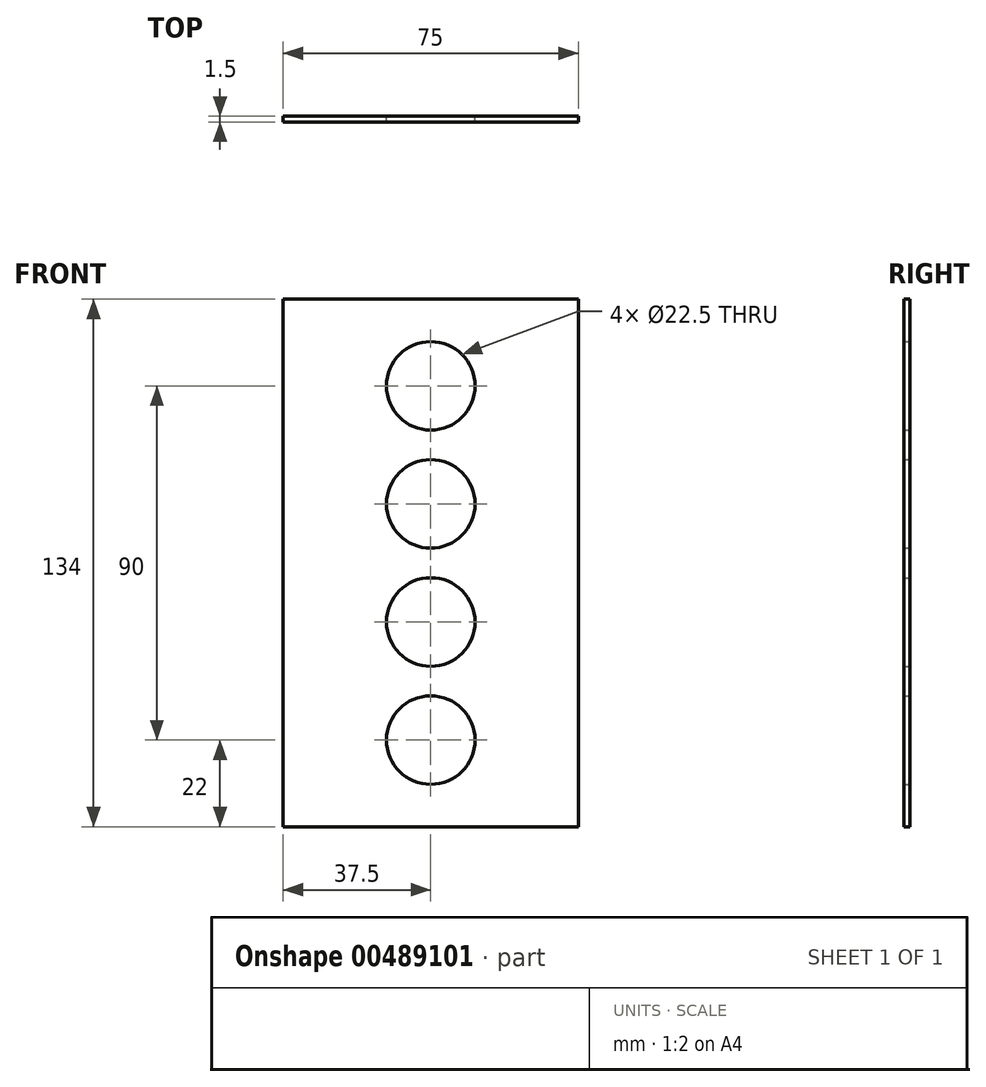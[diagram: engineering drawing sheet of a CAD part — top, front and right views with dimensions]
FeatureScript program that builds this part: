
annotation { "Feature Type Name" : "Feature", "Feature Type Description" : "" }
export const myFeature = defineFeature(function(context is Context, id is Id, definition is map)
    precondition{}
    {
        {
            var Q0;
            Q0=qCreatedBy(makeId("Front.planeOp"),FACE);
            var sketch = newSketch(context, id + "F0", { "sketchPlane" : qUnion([Q0])});
            skLineSegment(sketch, "E0.bottom", {"start": v(37.5, 67) * mm, "end": v(-37.5, 67) * mm});
            skLineSegment(sketch, "E0.top", {"start": v(37.5, -67) * mm, "end": v(-37.5, -67) * mm});
            skLineSegment(sketch, "E0.left", {"start": v(37.5, 67) * mm, "end": v(37.5, -67) * mm});
            skLineSegment(sketch, "E0.right", {"start": v(-37.5, 67) * mm, "end": v(-37.5, -67) * mm});
            skPoint(sketch, "E0.middle", {"position": v(0, 0) * mm});
            skCircle(sketch, "E1", {"center": v(0, 45) * mm, "radius": 11.25 * mm});
            skCircle(sketch, "E2", {"center": v(0, 15) * mm, "radius": 11.25 * mm});
            skCircle(sketch, "E3", {"center": v(0, -15) * mm, "radius": 11.25 * mm});
            skCircle(sketch, "E4", {"center": v(0, -45) * mm, "radius": 11.25 * mm});
            skSolve(sketch);
        }
        {
            var Q0;
            Q0 = qSketchRegion(id + "F0", true);
            var Q1;
            Q1=makeQuery(id+"F0.imprint","IMPRINT",FACE,{"disambiguationData":[TD([[makeQuery(id+"F0.imprint","IMPRINT",EDGE,{"derivedFrom":sQuery(id+"F0.wireOp",EDGE,"E0.bottom")}),1.0]])]});
            extrude(context, id + "F1", {"entities" : qUnion([Q0, Q1]), "depth" : 1.5 * mm});
        }
    });
